# Revit family: Tinka 26W
name_source: partatom
category: Lighting Fixtures
revit_build: Autodesk Revit 2016 (Build: 20150714_1515(x64)
units: mm (PartAtom-declared; Revit-internal decimal feet)

## family parameters
Cut with Voids When Loaded = No
Host = Face
Light Source = No
OmniClass Number = 23.80.70.11.14.21
OmniClass Title = Spots and Tracklight Specialties
Part Type = Normal
Room Calculation Point = No
Round Connector Dimension = Use Diameter
Shared = No

## types (2) — shared parameters
Beam Angle = 25°
CRI = 80
Casing Color = White
Cutout = -
Default Elevation = 1219 mm
Depth = -
Description = Tracklight, 3-Circuit Track
Dimensions = 130mm x 113mm
Dimmable = No
Directivity = Yes
Driver = Integrated
Housing Material = Aluminium
IP Code = IP20
Lamp = LED
Last Updated = 2.3.2016
Lifetime L70 = 50000h
Manufacturer = Winled Oy Ltd
Model = Tinka 26W
Operating Temperature Range = -20° to +40°C
Type Image = Tinka 26W.png
URL = www.winled.fi
Voltage = 230 V
Wattage Comments = 26W

## per-type parameters (varying)
| type | Color Temperature | Lumens Output | Product Number | Tinka 26W light |
| Tinka 26W, Neutral White, 230V - 53ER397N026E | 4000K | 2595lm | 53ER397N026E | Tinka26WlightNV : Tinka 26W light NW |
| Tinka 26W, Warm White, 230V - 53ER397L026E | 3000K | 2340lm | 53ER397L026E | Tinka26WlightNV : Tinka 26W light WW |

## geometry (parser evidence)
native form markers: Sweep x9
no freeform markers — native parametric forms only
